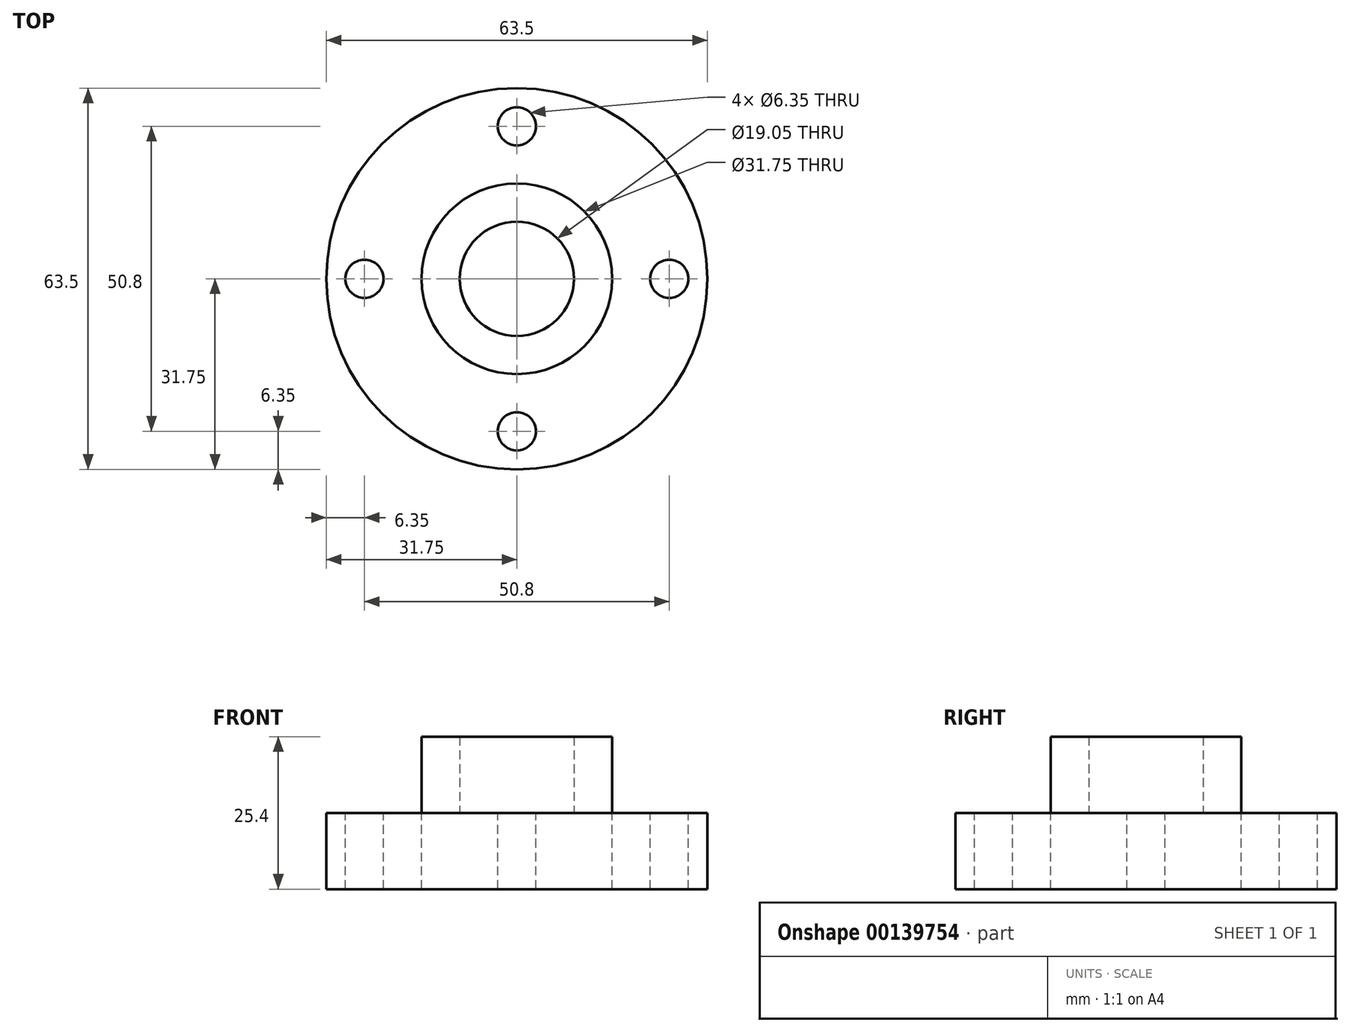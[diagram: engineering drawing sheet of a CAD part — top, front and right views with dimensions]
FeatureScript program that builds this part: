
annotation { "Feature Type Name" : "Feature", "Feature Type Description" : "" }
export const myFeature = defineFeature(function(context is Context, id is Id, definition is map)
    precondition{}
    {
        {
            var Q0;
            Q0=qCreatedBy(makeId("Top.planeOp"),FACE);
            var sketch = newSketch(context, id + "F0", { "sketchPlane" : qUnion([Q0])});
            skCircle(sketch, "E0", {"center": v(0, 0) * mm, "radius": 9.53 * mm});
            skCircle(sketch, "E1", {"center": v(0, 0) * mm, "radius": 15.88 * mm});
            skCircle(sketch, "E2", {"center": v(0, 0) * mm, "radius": 25.4 * mm, "construction": true});
            skCircle(sketch, "E3", {"center": v(0, 0) * mm, "radius": 31.75 * mm});
            skCircle(sketch, "E4", {"center": v(0, 25.4) * mm, "radius": 3.18 * mm});
            skCircle(sketch, "E5", {"center": v(25.4, 0) * mm, "radius": 3.18 * mm});
            skCircle(sketch, "E6", {"center": v(0, -25.4) * mm, "radius": 3.18 * mm});
            skCircle(sketch, "E7", {"center": v(-25.4, 0) * mm, "radius": 3.18 * mm});
            skSolve(sketch);
        }
        {
            var Q0;
            Q0=makeQuery(id+"F0.imprint","IMPRINT",FACE,{"disambiguationData":[TD([[makeQuery(id+"F0.imprint","IMPRINT",EDGE,{"derivedFrom":sQuery(id+"F0.wireOp",EDGE,"E1")}),-1.0]])]});
            extrude(context, id + "F1", {"entities" : qUnion([Q0]), "oppositeDirection" : true, "depth" : 12.7 * mm});
        }
        {
            var Q0;
            Q0=makeQuery(id+"F0.imprint","IMPRINT",FACE,{"disambiguationData":[TD([[makeQuery(id+"F0.imprint","IMPRINT",EDGE,{"derivedFrom":sQuery(id+"F0.wireOp",EDGE,"E0")}),-1.0]])]});
            extrude(context, id + "F2", {"entities" : qUnion([Q0]), "operationType" : NewBodyOperationType.ADD, "depth" : 12.7 * mm});
        }
        {
            var Q0;
            Q0=makeQuery(id+"F0.imprint","IMPRINT",FACE,{"disambiguationData":[TD([[makeQuery(id+"F0.imprint","IMPRINT",EDGE,{"derivedFrom":sQuery(id+"F0.wireOp",EDGE,"E0")}),1.0]])]});
            extrude(context, id + "F3", {"entities" : qUnion([Q0]), "operationType" : NewBodyOperationType.REMOVE, "endBound" : BoundingType.THROUGH_ALL, "oppositeDirection" : true, "depth" : 25.4 * mm});
        }
    });
